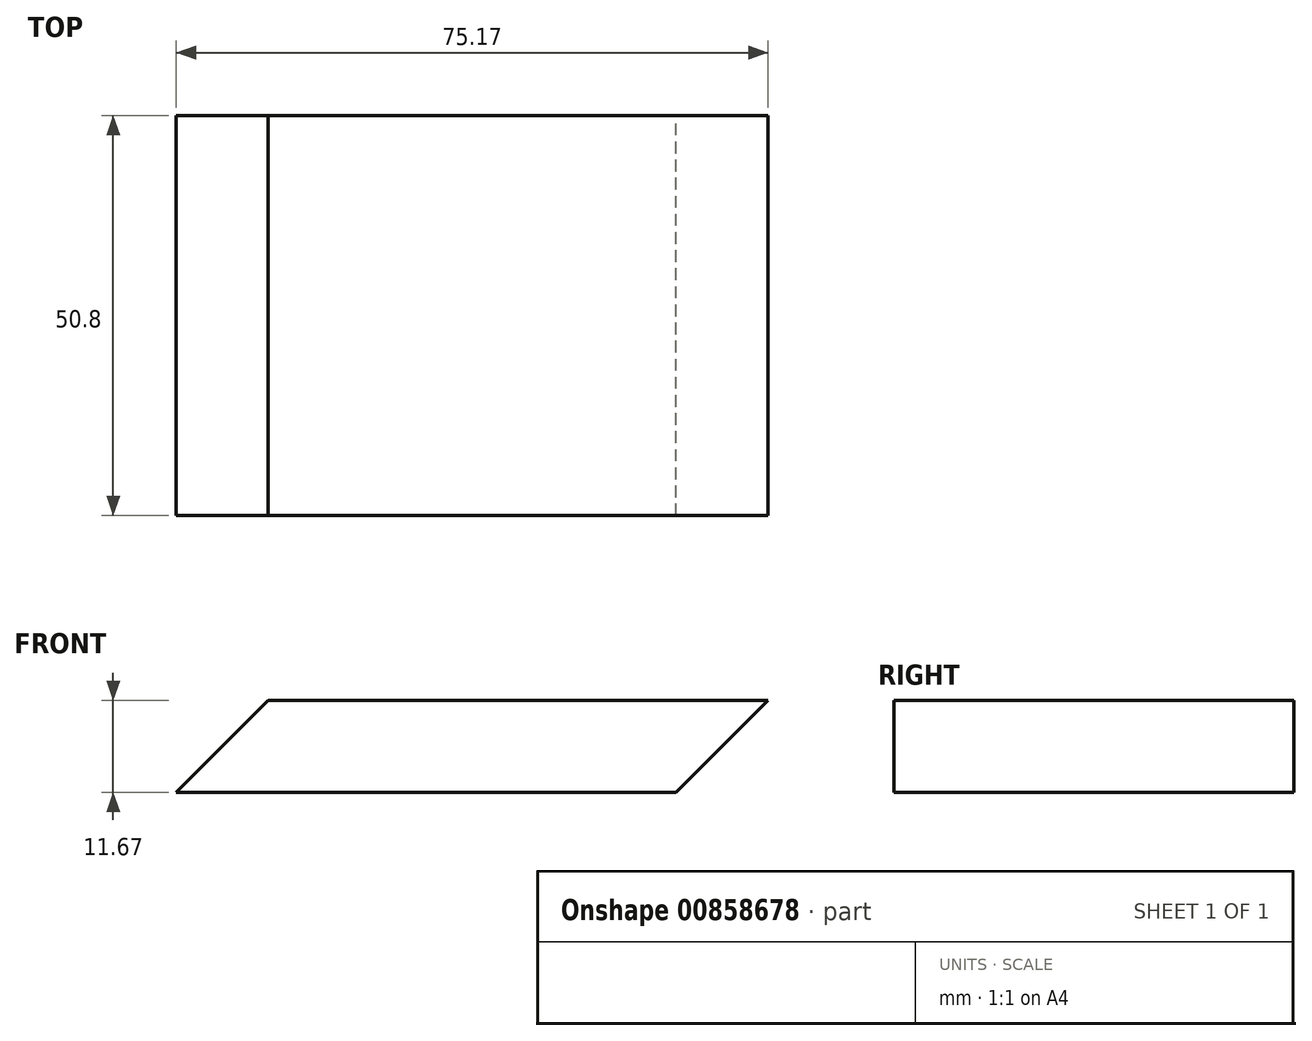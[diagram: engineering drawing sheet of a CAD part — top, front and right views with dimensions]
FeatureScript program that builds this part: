
annotation { "Feature Type Name" : "Feature", "Feature Type Description" : "" }
export const myFeature = defineFeature(function(context is Context, id is Id, definition is map)
    precondition{}
    {
        {
            var Q0;
            Q0=qCreatedBy(makeId("Front.planeOp"),FACE);
            var sketch = newSketch(context, id + "F0", { "sketchPlane" : qUnion([Q0])});
            skLineSegment(sketch, "E0", {"start": v(0, 0) * mm, "end": v(-63.5, 0) * mm});
            skLineSegment(sketch, "E1", {"start": v(-63.5, 0) * mm, "end": v(-51.83, 11.67) * mm});
            skLineSegment(sketch, "E2", {"start": v(-51.83, 11.67) * mm, "end": v(11.67, 11.67) * mm});
            skLineSegment(sketch, "E3", {"start": v(11.67, 11.67) * mm, "end": v(0, 0) * mm});
            skSolve(sketch);
        }
        {
            var Q0;
            Q0 = qSketchRegion(id + "F0", true);
            extrude(context, id + "F1", {"entities" : qUnion([Q0]), "depth" : 50.8 * mm, "offsetDistance" : 25.4 * mm});
        }
    });
